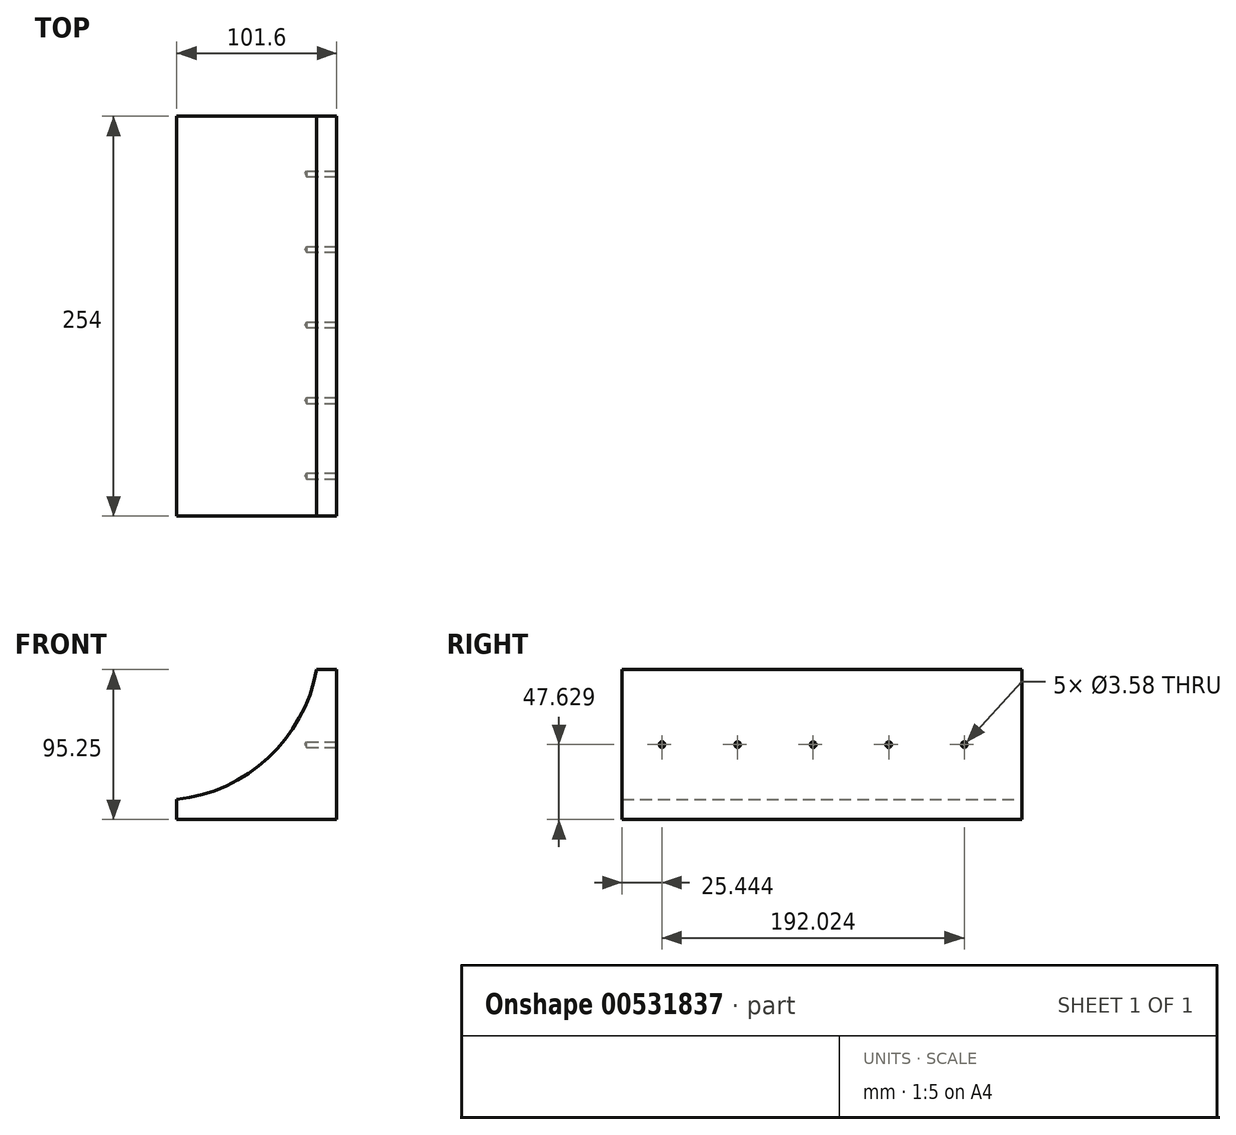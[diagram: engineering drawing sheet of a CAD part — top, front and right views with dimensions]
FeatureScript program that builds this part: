
annotation { "Feature Type Name" : "Feature", "Feature Type Description" : "" }
export const myFeature = defineFeature(function(context is Context, id is Id, definition is map)
    precondition{}
    {
        {
            var Q0;
            Q0=qCreatedBy(makeId("Front.planeOp"),FACE);
            var sketch = newSketch(context, id + "F0", { "sketchPlane" : qUnion([Q0])});
            skLineSegment(sketch, "E0.top", {"start": v(-39.78, -57.04) * mm, "end": v(48.44, -57.04) * mm});
            skLineSegment(sketch, "E1.bottom", {"start": v(49.12, 25.51) * mm, "end": v(61.82, 25.51) * mm});
            skLineSegment(sketch, "E1.top", {"start": v(49.12, -57.04) * mm, "end": v(61.82, -57.04) * mm});
            skLineSegment(sketch, "E1.left", {"start": v(61.82, 25.51) * mm, "end": v(61.82, -57.04) * mm});
            skLineSegment(sketch, "E1.right", {"start": v(49.12, 25.51) * mm, "end": v(49.12, -57.04) * mm});
            skLineSegment(sketch, "E2.bottom", {"start": v(-39.78, -57.04) * mm, "end": v(52.12, -56.76) * mm});
            skLineSegment(sketch, "E3.bottom", {"start": v(-39.78, -57.04) * mm, "end": v(55.47, -57.04) * mm});
            skArc(sketch, "E4", {"start": v(-39.78, -57.04) * mm, "mid": v(18.35, -30.49) * mm, "end": v(49.12, 25.51) * mm});
            skLineSegment(sketch, "E5.bottom", {"start": v(-39.78, -57.04) * mm, "end": v(61.82, -57.04) * mm});
            skLineSegment(sketch, "E5.top", {"start": v(-39.78, -69.74) * mm, "end": v(61.82, -69.74) * mm});
            skLineSegment(sketch, "E5.left", {"start": v(-39.78, -57.04) * mm, "end": v(-39.78, -69.74) * mm});
            skLineSegment(sketch, "E5.right", {"start": v(61.82, -57.04) * mm, "end": v(61.82, -69.74) * mm});
            skSolve(sketch);
        }
        {
            var Q0;
            Q0 = qSketchRegion(id + "F0", true);
            extrude(context, id + "F1", {"entities" : qUnion([Q0]), "depth" : 254 * mm, "offsetDistance" : 25.4 * mm});
        }
        {
            var Q0;
            Q0=makeQuery(id+"F1.opExtrude","SWEPT_FACE",FACE,{"disambiguationData":[OSD([sQuery(id+"F0.wireOp",EDGE,"E1.left"),sQuery(id+"F0.wireOp",EDGE,"E5.right")])]});
            var sketch = newSketch(context, id + "F2", { "sketchPlane" : qUnion([Q0])});
            skCircle(sketch, "E6", {"center": v(-228.56, -22.11) * mm, "radius": 1.78 * mm});
            skPoint(sketch, "E6.centerSnap0", {"position": v(-254, -22.11) * mm});
            skCircle(sketch, "E7.1.0.0", {"center": v(-180.55, -22.11) * mm, "radius": 1.78 * mm});
            skCircle(sketch, "E7.2.0.0", {"center": v(-132.54, -22.11) * mm, "radius": 1.78 * mm});
            skCircle(sketch, "E7.3.0.0", {"center": v(-84.54, -22.11) * mm, "radius": 1.78 * mm});
            skCircle(sketch, "E7.4.0.0", {"center": v(-36.53, -22.11) * mm, "radius": 1.78 * mm});
            skLineSegment(sketch, "E7.direction1", {"start": v(-228.56, -22.11) * mm, "end": v(-180.55, -22.11) * mm, "construction": true});
            skSolve(sketch);
        }
        {
            var Q0;
            Q0=sQuery(id+"F2.wireOp",VERTEX,"E6.center");
            var Q1;
            Q1=sQuery(id+"F2.wireOp",VERTEX,"E7.1.0.0.center");
            var Q2;
            Q2=sQuery(id+"F2.wireOp",VERTEX,"E7.2.0.0.center");
            var Q3;
            Q3=sQuery(id+"F2.wireOp",VERTEX,"E7.3.0.0.center");
            var Q4;
            Q4=sQuery(id+"F2.wireOp",VERTEX,"E7.4.0.0.center");
            var Q5;
            Q5=makeQuery(id+"F1.opExtrude","SWEPT_BODY",BODY,{"disambiguationData":[OSD([sQuery(id+"F0.wireOp",EDGE,"E1.bottom"),sQuery(id+"F0.wireOp",EDGE,"E1.left"),sQuery(id+"F0.wireOp",EDGE,"E4"),sQuery(id+"F0.wireOp",EDGE,"E5.top"),sQuery(id+"F0.wireOp",EDGE,"E5.left"),sQuery(id+"F0.wireOp",EDGE,"E5.right")])]});
            hole(context, id + "F3", {"style" : HoleStyle.SIMPLE, "endStyle" : HoleEndStyle.BLIND, "holeDiameter" : 3.58 * mm, "holeDepth" : 19.05 * mm, "isTappedThrough" : true, "tappedDepth" : 12.7 * mm, "tapClearance" : 3, "locations" : qUnion([Q0, Q1, Q2, Q3, Q4]), "scope" : qUnion([Q5])});
        }
    });
